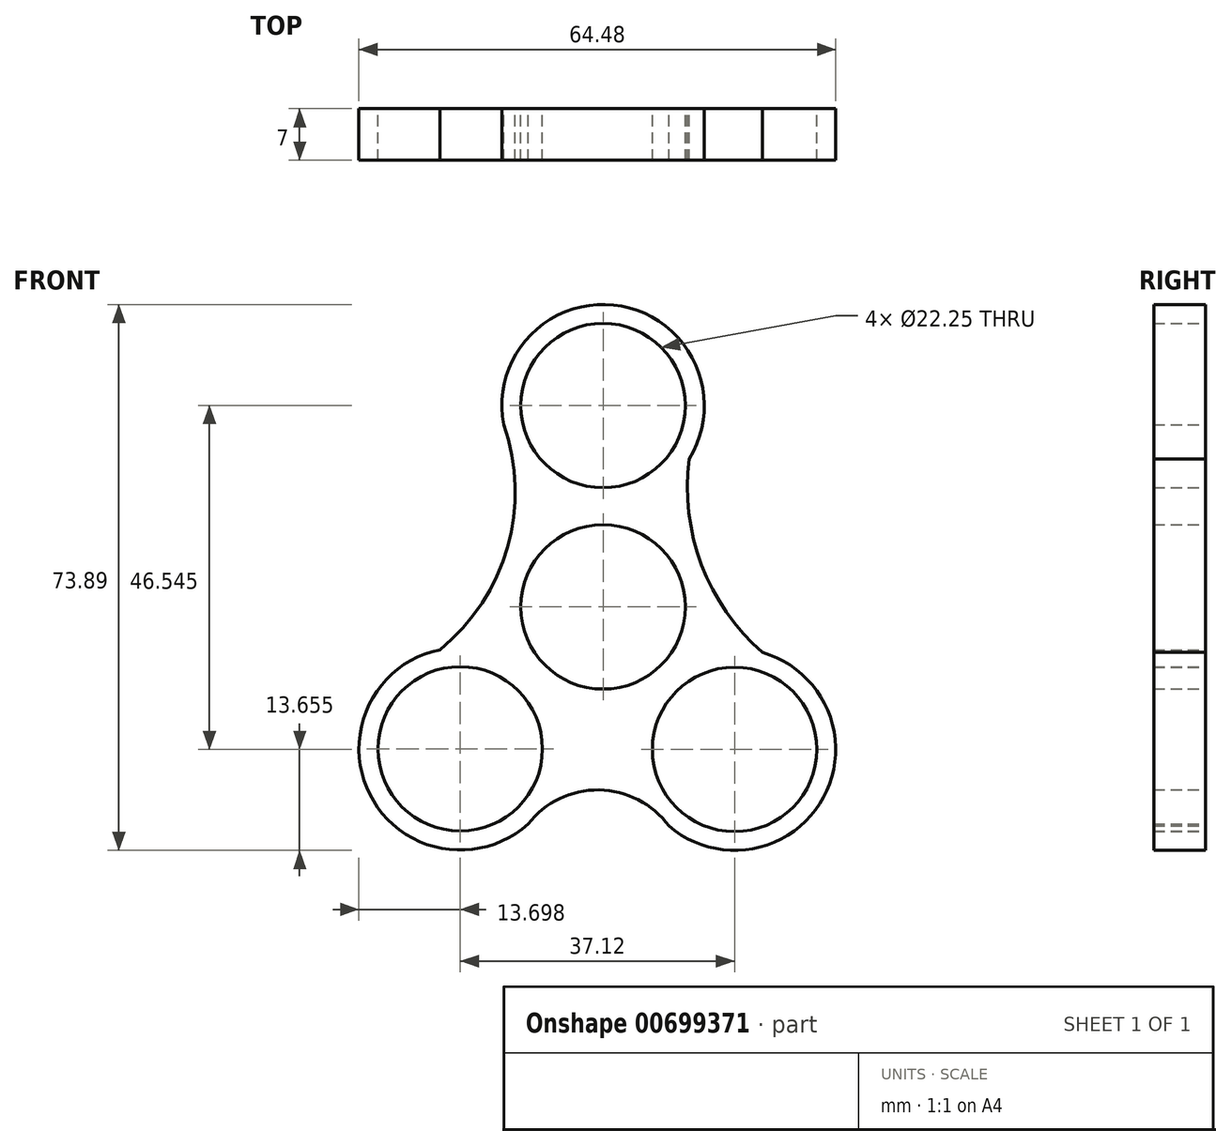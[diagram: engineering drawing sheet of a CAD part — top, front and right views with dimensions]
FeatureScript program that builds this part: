
annotation { "Feature Type Name" : "Feature", "Feature Type Description" : "" }
export const myFeature = defineFeature(function(context is Context, id is Id, definition is map)
    precondition{}
    {
        {
            var Q0;
            Q0=qCreatedBy(makeId("Front.planeOp"),FACE);
            var sketch = newSketch(context, id + "F0", { "sketchPlane" : qUnion([Q0])});
            skCircle(sketch, "E0", {"center": v(0, 0) * mm, "radius": 11.12 * mm});
            skCircle(sketch, "E1", {"center": v(0, 27.25) * mm, "radius": 11.12 * mm});
            skCircle(sketch, "E2", {"center": v(-19.32, -19.22) * mm, "radius": 11.12 * mm});
            skCircle(sketch, "E3", {"center": v(17.8, -19.3) * mm, "radius": 11.12 * mm});
            skCircle(sketch, "E4", {"center": v(0, 27.25) * mm, "radius": 13.69 * mm});
            skCircle(sketch, "E5", {"center": v(17.8, -19.3) * mm, "radius": 13.66 * mm});
            skCircle(sketch, "E6", {"center": v(-19.32, -19.22) * mm, "radius": 13.7 * mm});
            skLineSegment(sketch, "E7", {"start": v(-21.95, 27.25) * mm, "end": v(19.97, 27.25) * mm});
            skArc(sketch, "E8", {"start": v(11.64, 20.04) * mm, "mid": v(13.33, 5.7) * mm, "end": v(21.59, -6.17) * mm});
            skArc(sketch, "E9", {"start": v(-22.08, -5.8) * mm, "mid": v(-12.92, 8.06) * mm, "end": v(-13.44, 24.66) * mm});
            skArc(sketch, "E10", {"start": v(8.9, -29.66) * mm, "mid": v(-0.56, -24.78) * mm, "end": v(-10.15, -29.4) * mm});
            skSolve(sketch);
        }
        {
            var Q0;
            Q0=makeQuery(id+"F0.imprint","IMPRINT",FACE,{"disambiguationData":[TD([[makeQuery(id+"F0.imprint","IMPRINT",EDGE,{"derivedFrom":sQuery(id+"F0.wireOp",EDGE,"E0")}),-1.0]])]});
            var Q1;
            {var subQ0=sQuery(id+"F0.wireOp",EDGE,"E7");var subQ1=sQuery(id+"F0.wireOp",EDGE,"E1");var subQ2=makeQuery(id+"F0.imprint","INTERSECT",VERTEX,{"disambiguationData":[OD(0.0)],"derivedFrom":[subQ1,subQ0]});Q1=makeQuery(id+"F0.imprint","IMPRINT",FACE,{"disambiguationData":[TD([[makeQuery(id+"F0.imprint","IMPRINT",EDGE,{"disambiguationData":[TD([[subQ2,1.0]])],"derivedFrom":subQ1}),-1.0]])]});}
            var Q2;
            {var subQ2=sQuery(id+"F0.wireOp",EDGE,"E7");var subQ8=sQuery(id+"F0.wireOp",EDGE,"E1");var subQ9=makeQuery(id+"F0.imprint","INTERSECT",VERTEX,{"disambiguationData":[OD(0.0)],"derivedFrom":[subQ8,subQ2]});Q2=makeQuery(id+"F0.imprint","IMPRINT",FACE,{"disambiguationData":[TD([[makeQuery(id+"F0.imprint","IMPRINT",EDGE,{"disambiguationData":[TD([[subQ9,-1.0]])],"derivedFrom":subQ8}),-1.0]])]});}
            var Q3;
            Q3=makeQuery(id+"F0.imprint","IMPRINT",FACE,{"disambiguationData":[TD([[makeQuery(id+"F0.imprint","IMPRINT",EDGE,{"derivedFrom":sQuery(id+"F0.wireOp",EDGE,"E3")}),-1.0]])]});
            var Q4;
            Q4=makeQuery(id+"F0.imprint","IMPRINT",FACE,{"disambiguationData":[TD([[makeQuery(id+"F0.imprint","IMPRINT",EDGE,{"derivedFrom":sQuery(id+"F0.wireOp",EDGE,"E2")}),-1.0]])]});
            extrude(context, id + "F1", {"entities" : qUnion([Q0, Q1, Q2, Q3, Q4]), "depth" : 7 * mm, "offsetDistance" : 25 * mm});
        }
        {
            var Q0;
            Q0=qCreatedBy(makeId("Front.planeOp"),FACE);
            var sketch = newSketch(context, id + "F2", { "sketchPlane" : qUnion([Q0])});
            skText(sketch, "E11", { "text": "Lp", "fontName": "OpenSans-Regular.ttf"});
            const initialGuessF2  = {"E11": [0.0121, -0.006, 1, 0, 0.00404]};
            skSetInitialGuess(sketch, initialGuessF2);
            skSolve(sketch);
        }
        {
            var Q0;
            Q0 = qSketchRegion(id + "F2", true);
            extrude(context, id + "F3", {"entities" : qUnion([Q0]), "operationType" : NewBodyOperationType.ADD, "depth" : 7 * mm, "offsetDistance" : 25 * mm});
        }
        {
            var Q0;
            Q0=qCreatedBy(makeId("Front.planeOp"),FACE);
            var sketch = newSketch(context, id + "F4", { "sketchPlane" : qUnion([Q0])});
            skText(sketch, "E12", { "text": "Lp", "fontName": "OpenSans-Regular.ttf"});
            const initialGuessF4  = {"E12": [0.0106, -0.00658, 1, 0, 0.005]};
            skSetInitialGuess(sketch, initialGuessF4);
            skSolve(sketch);
        }
        {
            var Q0;
            Q0 = qSketchRegion(id + "F4", true);
            extrude(context, id + "F5", {"entities" : qUnion([Q0]), "operationType" : NewBodyOperationType.ADD, "depth" : 7 * mm, "offsetDistance" : 25 * mm});
        }
    });
